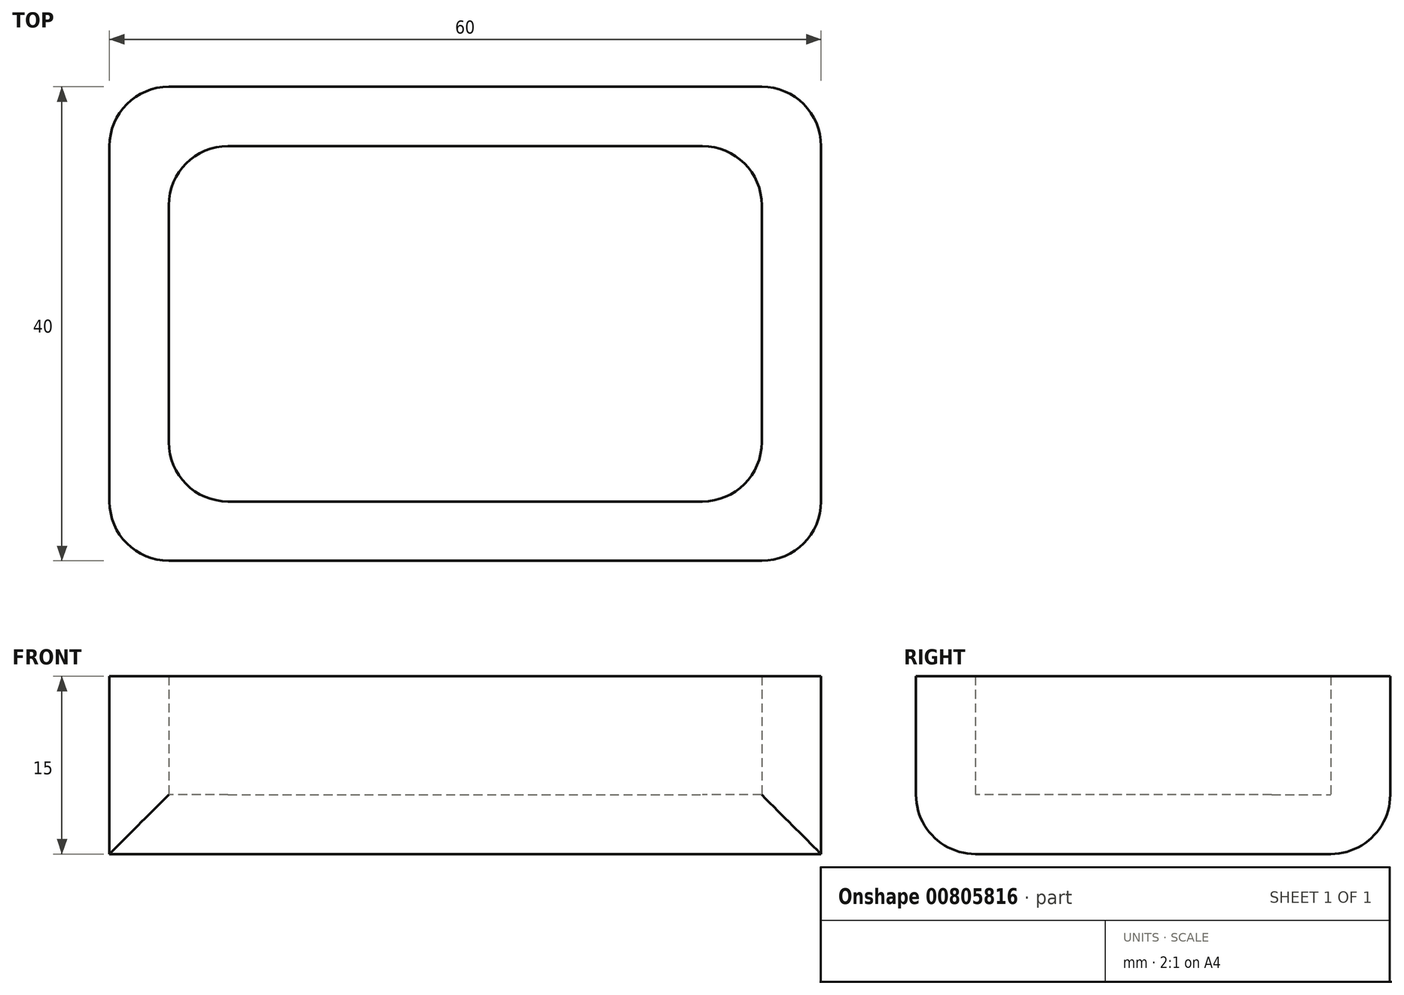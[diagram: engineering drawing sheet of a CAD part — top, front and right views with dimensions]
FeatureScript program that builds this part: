
annotation { "Feature Type Name" : "Feature", "Feature Type Description" : "" }
export const myFeature = defineFeature(function(context is Context, id is Id, definition is map)
    precondition{}
    {
        {
            var Q0;
            Q0=qCreatedBy(makeId("Top.planeOp"),FACE);
            var sketch = newSketch(context, id + "F0", { "sketchPlane" : qUnion([Q0])});
            skLineSegment(sketch, "E0.bottom", {"start": v(-30, 20) * mm, "end": v(30, 20) * mm});
            skLineSegment(sketch, "E0.top", {"start": v(-30, -20) * mm, "end": v(30, -20) * mm});
            skLineSegment(sketch, "E0.left", {"start": v(-30, 20) * mm, "end": v(-30, -20) * mm});
            skLineSegment(sketch, "E0.right", {"start": v(30, 20) * mm, "end": v(30, -20) * mm});
            skPoint(sketch, "E0.middle", {"position": v(0, 0) * mm});
            skSolve(sketch);
        }
        {
            var Q0;
            Q0=qSketchRegion(id+"F0",true);
            extrude(context, id + "F1", {"entities" : qUnion([Q0]), "depth" : 15 * mm, "offsetDistance" : 25 * mm});
        }
        {
            var Q0;
            Q0=makeQuery(id+"F1.opExtrude","CAP_FACE",FACE,{"disambiguationData":[OSD([sQuery(id+"F0.wireOp",EDGE,"E0.bottom"),sQuery(id+"F0.wireOp",EDGE,"E0.top"),sQuery(id+"F0.wireOp",EDGE,"E0.left"),sQuery(id+"F0.wireOp",EDGE,"E0.right")])],"isStart":false});
            shell(context, id + "F2", {"entities" : qUnion([Q0]), "thickness" : 5 * mm});
        }
        {
            var Q0;
            Q0=makeQuery(id+"F1.opExtrude","SWEPT_EDGE",EDGE,{"disambiguationData":[OSD([sQuery(id+"F0.wireOp",EDGE,"E0.bottom"),sQuery(id+"F0.wireOp",EDGE,"E0.left")])]});
            var Q1;
            Q1=makeQuery(id+"F1.opExtrude","SWEPT_EDGE",EDGE,{"disambiguationData":[OSD([sQuery(id+"F0.wireOp",EDGE,"E0.bottom"),sQuery(id+"F0.wireOp",EDGE,"E0.right")])]});
            var Q2;
            Q2=makeQuery(id+"F1.opExtrude","SWEPT_EDGE",EDGE,{"disambiguationData":[OSD([sQuery(id+"F0.wireOp",EDGE,"E0.top"),sQuery(id+"F0.wireOp",EDGE,"E0.left")])]});
            var Q3;
            Q3=makeQuery(id+"F1.opExtrude","SWEPT_EDGE",EDGE,{"disambiguationData":[OSD([sQuery(id+"F0.wireOp",EDGE,"E0.top"),sQuery(id+"F0.wireOp",EDGE,"E0.right")])]});
            var Q4;
            Q4=makeQuery(id+"F2.opShell","OFFSET_EDGE",EDGE,{"disambiguationData":[OSD([sQuery(id+"F0.wireOp",EDGE,"E0.top"),sQuery(id+"F0.wireOp",EDGE,"E0.left")])]});
            var Q5;
            Q5=makeQuery(id+"F2.opShell","OFFSET_EDGE",EDGE,{"disambiguationData":[OSD([sQuery(id+"F0.wireOp",EDGE,"E0.bottom"),sQuery(id+"F0.wireOp",EDGE,"E0.left")])]});
            var Q6;
            Q6=makeQuery(id+"F2.opShell","OFFSET_EDGE",EDGE,{"disambiguationData":[OSD([sQuery(id+"F0.wireOp",EDGE,"E0.top"),sQuery(id+"F0.wireOp",EDGE,"E0.right")])]});
            var Q7;
            Q7=makeQuery(id+"F2.opShell","OFFSET_EDGE",EDGE,{"disambiguationData":[OSD([sQuery(id+"F0.wireOp",EDGE,"E0.bottom"),sQuery(id+"F0.wireOp",EDGE,"E0.right")])]});
            var Q8;
            Q8=makeQuery(id+"F1.opExtrude","CAP_EDGE",EDGE,{"disambiguationData":[OSD([sQuery(id+"F0.wireOp",EDGE,"E0.bottom")])],"isStart":true});
            var Q9;
            Q9=makeQuery(id+"F1.opExtrude","CAP_EDGE",EDGE,{"disambiguationData":[OSD([sQuery(id+"F0.wireOp",EDGE,"E0.top")])],"isStart":true});
            fillet(context, id + "F3", {"entities" : qUnion([Q0, Q1, Q2, Q3, Q4, Q5, Q6, Q7, Q8, Q9]), "radius" : 5 * mm, "tangentPropagation" : true, "allowEdgeOverflow" : false});
        }
    });
